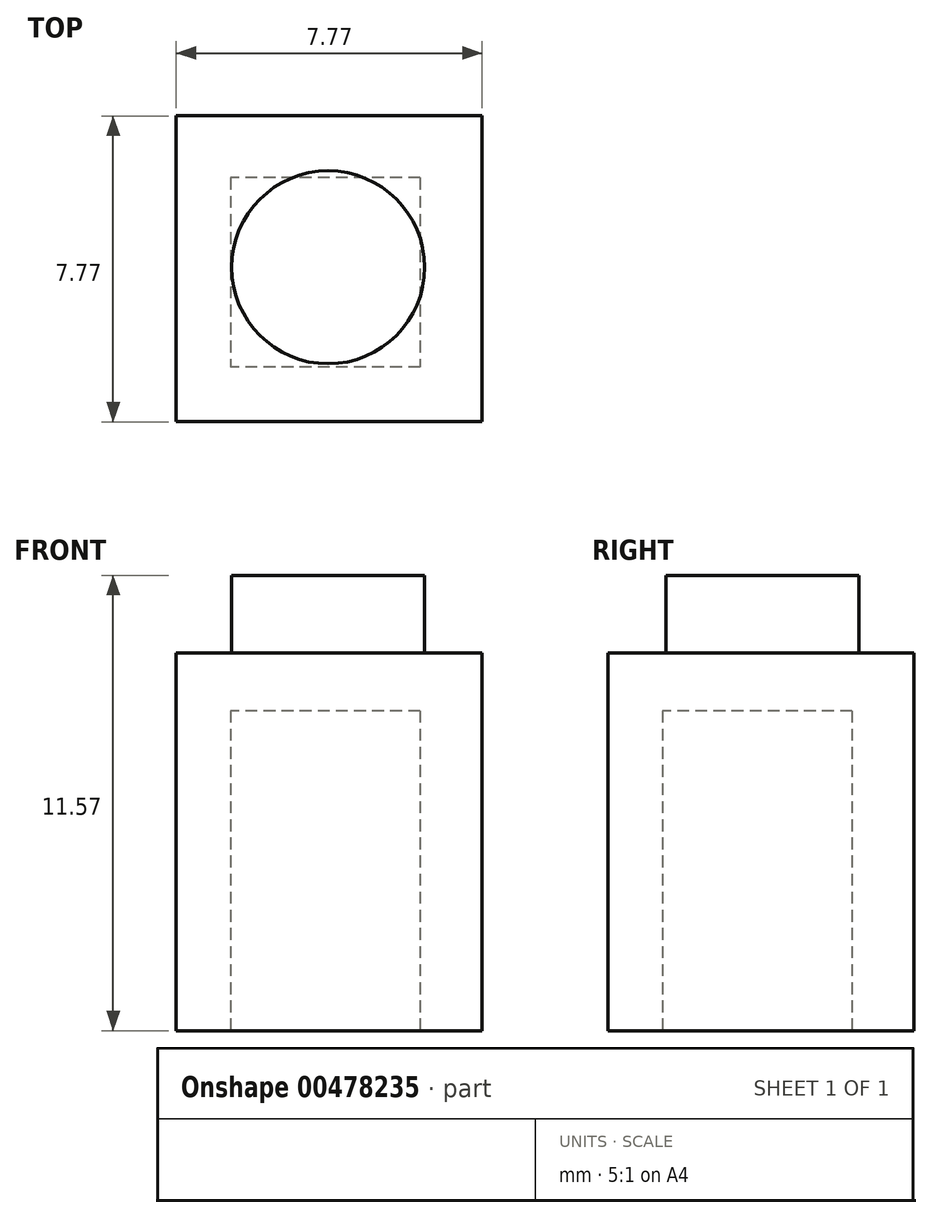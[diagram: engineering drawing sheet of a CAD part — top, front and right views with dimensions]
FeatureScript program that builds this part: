
annotation { "Feature Type Name" : "Feature", "Feature Type Description" : "" }
export const myFeature = defineFeature(function(context is Context, id is Id, definition is map)
    precondition{}
    {
        {
            var Q0;
            Q0=qCreatedBy(makeId("Top.planeOp"),FACE);
            var sketch = newSketch(context, id + "F0", { "sketchPlane" : qUnion([Q0])});
            skLineSegment(sketch, "E0.bottom", {"start": v(-10.5, 28.51) * mm, "end": v(-2.73, 28.51) * mm});
            skLineSegment(sketch, "E0.top", {"start": v(-10.5, 20.74) * mm, "end": v(-2.73, 20.74) * mm});
            skLineSegment(sketch, "E0.left", {"start": v(-10.5, 28.51) * mm, "end": v(-10.5, 20.74) * mm});
            skLineSegment(sketch, "E0.right", {"start": v(-2.73, 28.51) * mm, "end": v(-2.73, 20.74) * mm});
            skSolve(sketch);
        }
        {
            var Q0;
            Q0=makeQuery(id+"F0.imprint","IMPRINT",FACE,{"disambiguationData":[TD([[makeQuery(id+"F0.imprint","IMPRINT",EDGE,{"derivedFrom":sQuery(id+"F0.wireOp",EDGE,"E0.bottom")}),-1.0]])]});
            extrude(context, id + "F1", {"entities" : qUnion([Q0]), "depth" : 9.6 * mm});
        }
        {
            var Q0;
            Q0=makeQuery(id+"F1.opExtrude","CAP_FACE",FACE,{"disambiguationData":[OSD([sQuery(id+"F0.wireOp",EDGE,"E0.bottom"),sQuery(id+"F0.wireOp",EDGE,"E0.top"),sQuery(id+"F0.wireOp",EDGE,"E0.left"),sQuery(id+"F0.wireOp",EDGE,"E0.right")])],"isStart":false});
            var sketch = newSketch(context, id + "F2", { "sketchPlane" : qUnion([Q0])});
            skCircle(sketch, "E1", {"center": v(-6.64, 24.66) * mm, "radius": 2.45 * mm});
            skSolve(sketch);
        }
        {
            var Q0;
            Q0=makeQuery(id+"F2.imprint","IMPRINT",FACE,{"disambiguationData":[TD([[makeQuery(id+"F2.imprint","IMPRINT",EDGE,{"derivedFrom":sQuery(id+"F2.wireOp",EDGE,"E1")}),1.0]])]});
            extrude(context, id + "F3", {"entities" : qUnion([Q0]), "operationType" : NewBodyOperationType.ADD, "depth" : 1.97 * mm});
        }
        {
            var Q0;
            Q0=makeQuery(id+"F1.opExtrude","CAP_FACE",FACE,{"disambiguationData":[OSD([sQuery(id+"F0.wireOp",EDGE,"E0.bottom"),sQuery(id+"F0.wireOp",EDGE,"E0.top"),sQuery(id+"F0.wireOp",EDGE,"E0.left"),sQuery(id+"F0.wireOp",EDGE,"E0.right")])],"isStart":true});
            var sketch = newSketch(context, id + "F4", { "sketchPlane" : qUnion([Q0])});
            skLineSegment(sketch, "E2.bottom", {"start": v(-4.3, -26.94) * mm, "end": v(-9.12, -26.94) * mm});
            skLineSegment(sketch, "E2.top", {"start": v(-4.3, -22.12) * mm, "end": v(-9.12, -22.12) * mm});
            skLineSegment(sketch, "E2.left", {"start": v(-4.3, -26.94) * mm, "end": v(-4.3, -22.12) * mm});
            skLineSegment(sketch, "E2.right", {"start": v(-9.12, -26.94) * mm, "end": v(-9.12, -22.12) * mm});
            skSolve(sketch);
        }
        {
            var Q0;
            Q0=makeQuery(id+"F4.imprint","IMPRINT",FACE,{"disambiguationData":[TD([[makeQuery(id+"F4.imprint","IMPRINT",EDGE,{"derivedFrom":sQuery(id+"F4.wireOp",EDGE,"E2.bottom")}),-1.0]])]});
            extrude(context, id + "F5", {"entities" : qUnion([Q0]), "operationType" : NewBodyOperationType.REMOVE, "oppositeDirection" : true, "depth" : 8.13 * mm});
        }
    });
